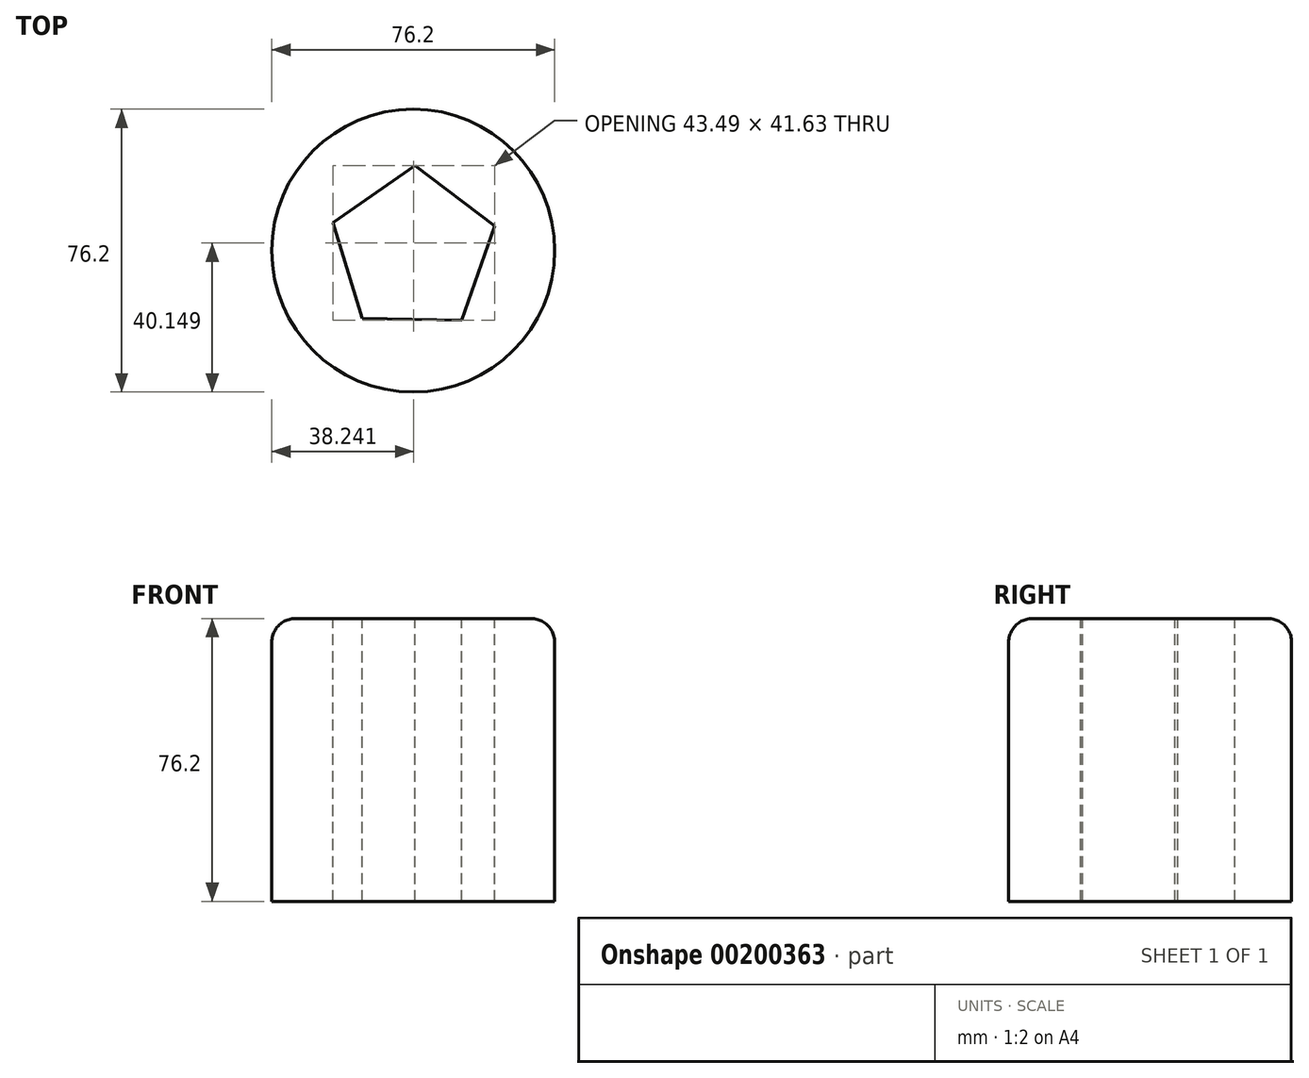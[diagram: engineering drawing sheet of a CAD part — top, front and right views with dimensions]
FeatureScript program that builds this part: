
annotation { "Feature Type Name" : "Feature", "Feature Type Description" : "" }
export const myFeature = defineFeature(function(context is Context, id is Id, definition is map)
    precondition{}
    {
        {
            var Q0;
            Q0=qCreatedBy(makeId("Top.planeOp"),FACE);
            var sketch = newSketch(context, id + "F0", { "sketchPlane" : qUnion([Q0])});
            skCircle(sketch, "E0", {"center": v(0, 0) * mm, "radius": 38.1 * mm});
            skSolve(sketch);
        }
        {
            var Q0;
            Q0=makeQuery(id+"F0.imprint","IMPRINT",FACE,{"disambiguationData":[TD([[makeQuery(id+"F0.imprint","IMPRINT",EDGE,{"derivedFrom":sQuery(id+"F0.wireOp",EDGE,"E0")}),1.0]])]});
            extrude(context, id + "F1", {"entities" : qUnion([Q0]), "depth" : 76.2 * mm});
        }
        {
            var Q0;
            Q0=makeQuery(id+"F1.opExtrude","CAP_FACE",FACE,{"disambiguationData":[OSD([sQuery(id+"F0.wireOp",EDGE,"E0")])],"isStart":false});
            var sketch = newSketch(context, id + "F2", { "sketchPlane" : qUnion([Q0])});
            skCircle(sketch, "E1.cCircle", {"center": v(0, 0) * mm, "radius": 18.5 * mm, "construction": true});
            skLineSegment(sketch, "E1.0", {"start": v(-21.6, 7.5) * mm, "end": v(0.46, 22.86) * mm});
            skLineSegment(sketch, "E1.1", {"start": v(0.46, 22.86) * mm, "end": v(21.88, 6.63) * mm});
            skLineSegment(sketch, "E1.2", {"start": v(21.88, 6.63) * mm, "end": v(13.07, -18.76) * mm});
            skLineSegment(sketch, "E1.3", {"start": v(13.07, -18.76) * mm, "end": v(-13.8, -18.23) * mm});
            skLineSegment(sketch, "E1.4", {"start": v(-13.8, -18.23) * mm, "end": v(-21.6, 7.5) * mm});
            skPoint(sketch, "E1.0.midPoint", {"position": v(-10.57, 15.18) * mm});
            skSolve(sketch);
        }
        {
            var Q0;
            Q0 = qSketchRegion(id + "F2", true);
            extrude(context, id + "F3", {"entities" : qUnion([Q0]), "operationType" : NewBodyOperationType.REMOVE, "endBound" : BoundingType.THROUGH_ALL, "oppositeDirection" : true, "depth" : 60.7 * mm});
        }
        {
            var Q0;
            Q0=makeQuery(id+"F1.opExtrude","CAP_EDGE",EDGE,{"disambiguationData":[OSD([sQuery(id+"F0.wireOp",EDGE,"E0")])],"isStart":false});
            fillet(context, id + "F4", {"entities" : qUnion([Q0]), "radius" : 6.35 * mm, "tangentPropagation" : true, "allowEdgeOverflow" : false});
        }
    });
